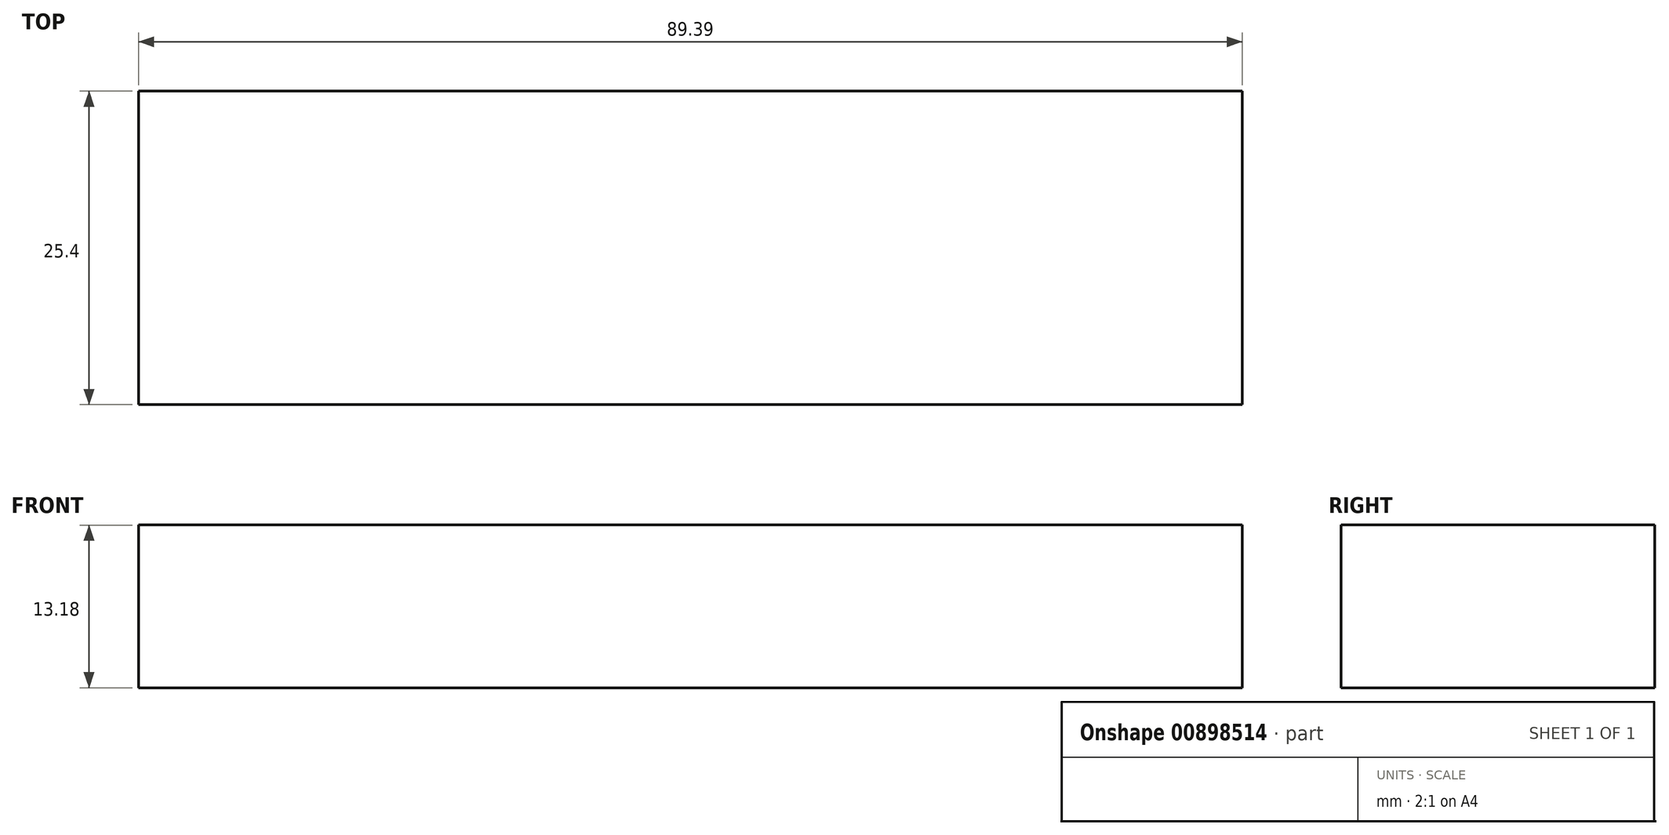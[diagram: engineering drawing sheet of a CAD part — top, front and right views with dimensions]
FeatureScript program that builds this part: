
annotation { "Feature Type Name" : "Feature", "Feature Type Description" : "" }
export const myFeature = defineFeature(function(context is Context, id is Id, definition is map)
    precondition{}
    {
        {
            var Q0;
            Q0=qCreatedBy(makeId("Front.planeOp"),FACE);
            var sketch = newSketch(context, id + "F0", { "sketchPlane" : qUnion([Q0])});
            skLineSegment(sketch, "E0.bottom", {"start": v(-99.49, 15.14) * mm, "end": v(-10.1, 15.14) * mm});
            skLineSegment(sketch, "E0.top", {"start": v(-99.49, 1.96) * mm, "end": v(-10.1, 1.96) * mm});
            skLineSegment(sketch, "E0.left", {"start": v(-99.49, 15.14) * mm, "end": v(-99.49, 1.96) * mm});
            skLineSegment(sketch, "E0.right", {"start": v(-10.1, 15.14) * mm, "end": v(-10.1, 1.96) * mm});
            skSolve(sketch);
        }
        {
            var Q0;
            Q0 = qSketchRegion(id + "F0", true);
            extrude(context, id + "F1", {"entities" : qUnion([Q0]), "depth" : 25.4 * mm, "offsetDistance" : 25.4 * mm});
        }
    });
